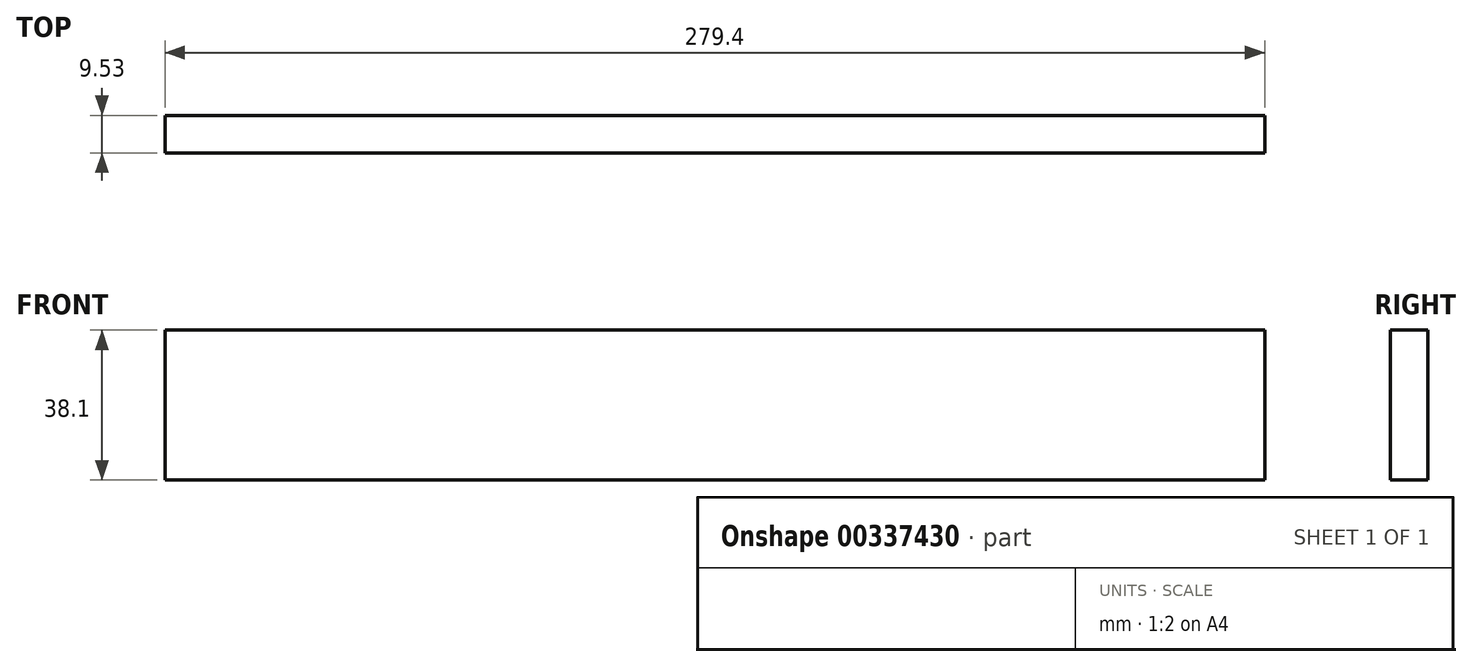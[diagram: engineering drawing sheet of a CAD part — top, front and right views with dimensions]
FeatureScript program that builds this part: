
annotation { "Feature Type Name" : "Feature", "Feature Type Description" : "" }
export const myFeature = defineFeature(function(context is Context, id is Id, definition is map)
    precondition{}
    {
        {
            var Q0;
            Q0=qCreatedBy(makeId("Front.planeOp"),FACE);
            var sketch = newSketch(context, id + "F0", { "sketchPlane" : qUnion([Q0])});
            skLineSegment(sketch, "E0.bottom", {"start": v(139.7, 19.05) * mm, "end": v(-139.7, 19.05) * mm});
            skLineSegment(sketch, "E0.top", {"start": v(139.7, -19.05) * mm, "end": v(-139.7, -19.05) * mm});
            skLineSegment(sketch, "E0.left", {"start": v(139.7, 19.05) * mm, "end": v(139.7, -19.05) * mm});
            skLineSegment(sketch, "E0.right", {"start": v(-139.7, 19.05) * mm, "end": v(-139.7, -19.05) * mm});
            skPoint(sketch, "E0.middle", {"position": v(0, 0) * mm});
            skSolve(sketch);
        }
        {
            var Q0;
            Q0 = qSketchRegion(id + "F0", true);
            extrude(context, id + "F1", {"entities" : qUnion([Q0]), "depth" : 9.52 * mm});
        }
    });
